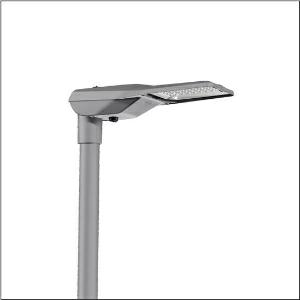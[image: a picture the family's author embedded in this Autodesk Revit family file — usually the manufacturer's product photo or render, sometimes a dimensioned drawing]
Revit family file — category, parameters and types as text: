
# Revit family: streetlight_sl_21_iq_mini___st0_8a_5xe2c31y08gb_e7ef
name_source: partatom
category: Lighting Fixtures
units: mm (PartAtom-declared; Revit-internal decimal feet)

## family parameters
Cut with Voids When Loaded = No
Host = Face
Light Source = No
Part Type = Normal
Room Calculation Point = No
Round Connector Dimension = Use Diameter
Shared = No

## types (1)
- --- (1 x LED, 5990 lm, 39.8 W, 3000K)
    Apparent Load = 40 VA
    CIE Flux Codes = 38 75 97 100 100
    Color Rendering = 70
    Color Temperature = 3000K
    Default Elevation = 1800 mm
    Description = Streetlight SL 21 iQ mini, mast luminaire, primary light control with lens, of PMMA, primary optical cover: cover, of toughened safety glass, transparent, light distribution: ST0.8a, light emission: direct distribution, primary light characteristic: asymmetric, installation type: post-top, side-entry, LED, High Power LED, rated luminous flux: 5.990lm, luminous efficacy: 151lm/W, light colour: 730, colour temperature: 3000K, control gear: iQ-Street Remote, D4i with power reduction, control: pre-setting: logarithmic dimming characteristic, Street-Remote, Auto-Match, Temp-Guard, Lumen-Switch, Night-Set, Smart-Wire, Light-Fading, Desk-Remote (wireless, voltage-free reading and setting of iQ features in the workshop via application-optimized NFC function/RFID function), optimised constant luminous flux control (CLO 2.0), mains connection: 220..240V, AC, 50/60Hz, start of lifetime: 40W, end of service life: 41W, reduction: 18W, luminaire housing, of diecast aluminium, powder-coated, SITECO metallic grey (DB 702S), corrosivity category C5 high according to DIN EN ISO 12944, please order mast flange separately, inclination adjustable: 0°, 5°, 10°, 15°, sealing non-destructively replaceable, multi-level sealing system, length: 628mm, width: 235mm, height: 110mm, mast flange for spigot size: 42mm (side-entry): 5XC10008XM4, 60/48mm (side-entry/post-top): 5XC10108XM2, 76/60mm (side-entry/post-top): 5XC10108XM1, mounting height: 4..8m, Smart Interface below and above, protection rating (complete): IP66, insulation class (complete): insulation class II (safety insulation), certification: CE, ENEC, ENEC+, VDE, impact resistance: IK10, permissible operating ambient temperature for outdoor applications: -40..+50°C, standard-compliant lighting for roads and squares, packaging unit: 1 piece

Light Distribution: ST0.8a
    Height = 110 mm
    Lamp = 1 x LED
    Lamp Light Flux = 5990 lm
    Lamp Power = 39.8 W
    Lamp count = 1
    Length = 625 mm
    Luminous efficacy = 151 lm/W
    Manufacturer = Siteco
    ModVariant = No
    Model = 5XE2C31Y08GB
    Mounting Place = Pole
    Mounting Type = Pole top
    Number of Poles = 1
    OnlyDefault = Yes
    Power Factor = 1
    Product Name = Streetlight SL 21 iQ mini | ST0.8a
    Product group = mast luminaire | pylon top
    ProductGroupID = 6100
    Protection Class = Protection class II
    Protection Degree = IP 66
    RLX_Detail_Level = 1
    RLX_Emergency_Light_Flux = 0 lm
    RLX_Emergency_Type = 0
    RLX_Emergency_Type_DB = No
    RlxData = <blob elided: 92761 chars, md5=79fd45ac>
    Socket = socket
    Standby Power = 0 W
    System Light Flux = 5990 lm
    System Power = 40 W
    Type Comments = factory setting: luminous flux: 100 % | dim-lin: 254 | 800 mA
    Type Image = l_1003514.jpg
    URL = http://relux.com
    VarID = @adj_115025
    Voltage = 0 V
    Weight = 0.00 kg
    Width = 234 mm

## geometry (parser evidence)
native form markers: Blend x4, Sweep x10
no freeform markers — native parametric forms only
